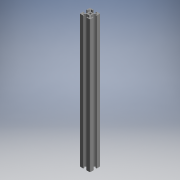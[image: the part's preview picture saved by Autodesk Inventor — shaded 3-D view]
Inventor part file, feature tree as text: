
AUTODESK INVENTOR PART (.ipt)
format: ipt  version: 2017.3 (Build 213256000, 256)  size: 207,872 bytes
history: native  units: mm (DEFAULTED — no unit token found)
features: other x7, sketch x2, extrude x1, hole x1
ambient origin geometry x8: Origin, YZ Plane, XZ Plane, XY Plane, X Axis, Y Axis, Z Axis, Center Point
bodies: Solid1 (feature_tree)
feature tree (11):
  extrude  "Extrusion1"  TaperAngle=0.0deg  [1 undecoded]
  hole  "Hole1"  [1 undecoded]
  other  "C1_XY"
  other  "C1_YZ"
  other  "C1_ZX"
  other  "C1_X"
  other  "C1_Y"
  other  "C1_Z"
  other  "C1_Center"
  sketch  "Sketch_75"  dims[d2=4.2mm d3=6.0mm d4=4.0mm d5=2.0mm d6=90.0deg d7=260.0mm d8=0.0mm d9=0.0mm]
  sketch  "Sketch2"  dims[d0=260.0mm d1=0.0mm]
note: 2 required parameter values undecoded (feature->parameter linkage not recoverable at this tier; creation-order binding heuristic only, values carry confidence <= 0.55)
